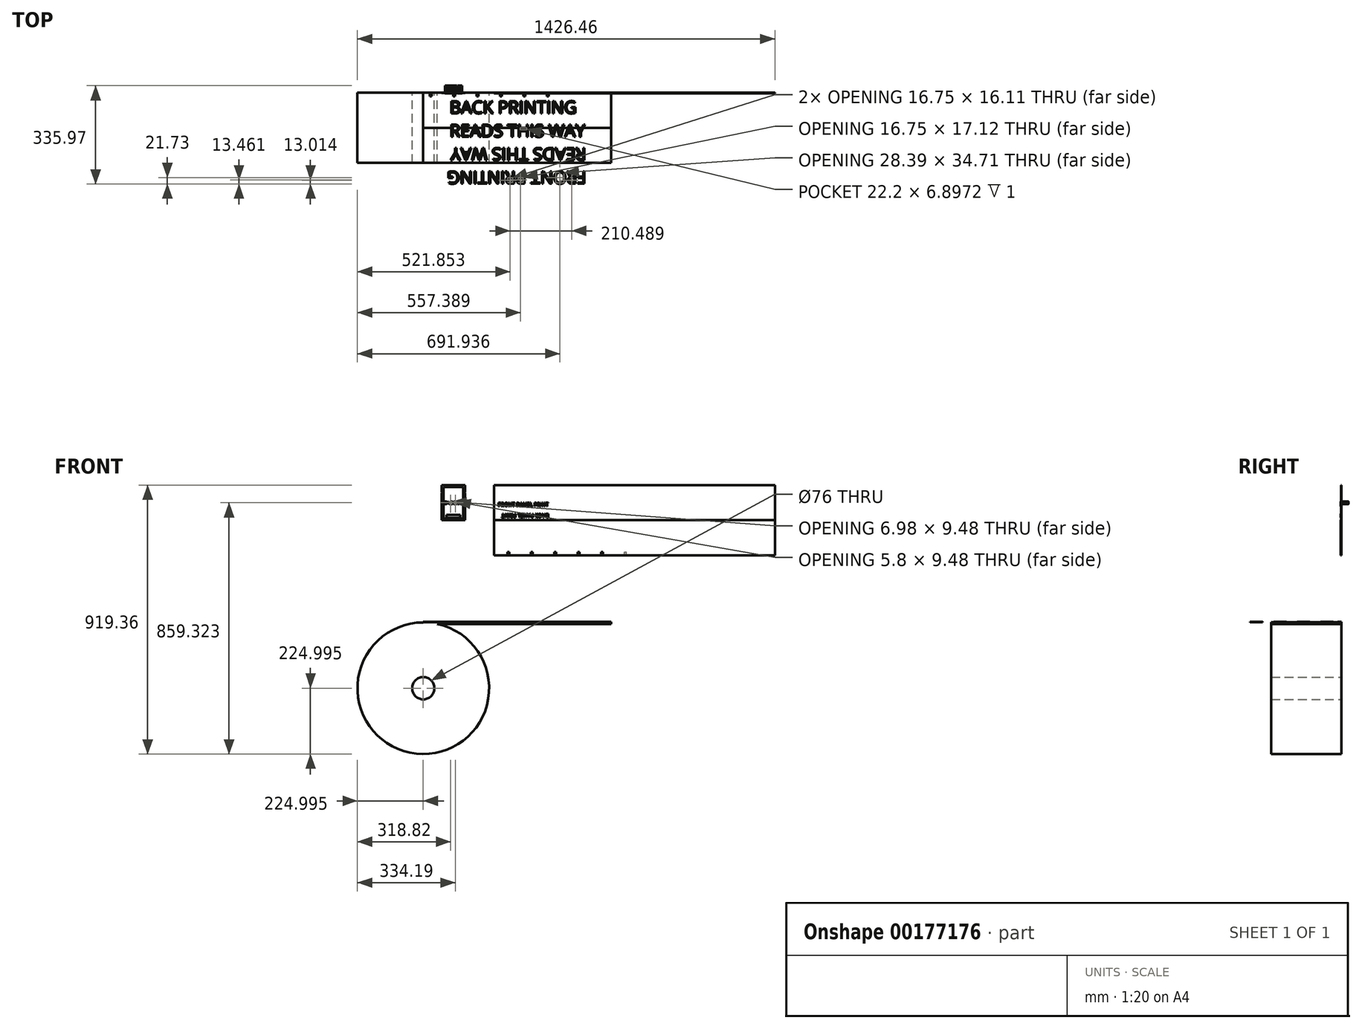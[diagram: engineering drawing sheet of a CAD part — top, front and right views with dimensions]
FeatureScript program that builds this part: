
annotation { "Feature Type Name" : "Feature", "Feature Type Description" : "" }
export const myFeature = defineFeature(function(context is Context, id is Id, definition is map)
    precondition{}
    {
        {
            assignVariable(context, id + "F0", {"name" : "hoogte", "anyValue" : 120});
        }
        {
            var Q0;
            Q0=qCreatedBy(makeId("Front.planeOp"),FACE);
            var sketch = newSketch(context, id + "F1", { "sketchPlane" : qUnion([Q0])});
            skLineSegment(sketch, "E0.bottom", {"start": v(-40, 60) * mm, "end": v(40, 60) * mm});
            skLineSegment(sketch, "E0.top", {"start": v(-40, -60) * mm, "end": v(40, -60) * mm});
            skLineSegment(sketch, "E0.left", {"start": v(-40, 60) * mm, "end": v(-40, -60) * mm});
            skLineSegment(sketch, "E0.right", {"start": v(40, 60) * mm, "end": v(40, -60) * mm});
            skLineSegment(sketch, "E1", {"start": v(-40, 36.41) * mm, "end": v(-38.59, 35) * mm});
            skLineSegment(sketch, "E2", {"start": v(-38.59, 35) * mm, "end": v(-40, 33.59) * mm});
            skLineSegment(sketch, "E3", {"start": v(40, 36.41) * mm, "end": v(38.59, 35) * mm});
            skLineSegment(sketch, "E4", {"start": v(38.59, 35) * mm, "end": v(40, 33.59) * mm});
            skLineSegment(sketch, "E5.bottom", {"start": v(138.46, 60) * mm, "end": v(1098.46, 60) * mm});
            skLineSegment(sketch, "E5.top", {"start": v(138.46, -180) * mm, "end": v(1098.46, -180) * mm});
            skLineSegment(sketch, "E5.left", {"start": v(138.46, 60) * mm, "end": v(138.46, -180) * mm});
            skLineSegment(sketch, "E5.right", {"start": v(1098.46, 60) * mm, "end": v(1098.46, -180) * mm});
            skLineSegment(sketch, "E6", {"start": v(138.46, -60) * mm, "end": v(1098.46, -60) * mm});
            skLineSegment(sketch, "E7", {"start": v(-40, 60) * mm, "end": v(40, -60) * mm, "construction": true});
            skLineSegment(sketch, "E8", {"start": v(40, 60) * mm, "end": v(-40, -60) * mm, "construction": true});
            skPoint(sketch, "E9", {"position": v(0, 0) * mm});
            skSolve(sketch);
        }
        {
            var Q0;
            {var subQ3=sQuery(id+"F1.wireOp",EDGE,"E0.bottom");Q0=makeQuery(id+"F1.imprint","IMPRINT",FACE,{"disambiguationData":[TD([[makeQuery(id+"F1.imprint","IMPRINT",EDGE,{"derivedFrom":subQ3}),-1.0]])]});}
            var Q1;
            Q1=makeQuery(id+"F1.imprint","IMPRINT",FACE,{"disambiguationData":[TD([[makeQuery(id+"F1.imprint","IMPRINT",EDGE,{"derivedFrom":sQuery(id+"F1.wireOp",EDGE,"E5.bottom")}),-1.0]])]});
            var Q2;
            {var subQ0=sQuery(id+"F1.wireOp",EDGE,"E5.top");Q2=makeQuery(id+"F1.imprint","IMPRINT",FACE,{"disambiguationData":[TD([[makeQuery(id+"F1.imprint","IMPRINT",EDGE,{"derivedFrom":subQ0}),1.0]])]});}
            extrude(context, id + "F2", {"entities" : qUnion([Q0, Q1, Q2]), "depth" : 1 * mm});
        }
        {
            var Q0;
            Q0=makeQuery(id+"F2.opExtrude","CAP_FACE",FACE,{"disambiguationData":[OSD([sQuery(id+"F1.wireOp",EDGE,"E0.bottom"),sQuery(id+"F1.wireOp",EDGE,"E0.top"),sQuery(id+"F1.wireOp",EDGE,"E0.left"),sQuery(id+"F1.wireOp",EDGE,"E0.right"),sQuery(id+"F1.wireOp",EDGE,"E1"),sQuery(id+"F1.wireOp",EDGE,"E2"),sQuery(id+"F1.wireOp",EDGE,"E3"),sQuery(id+"F1.wireOp",EDGE,"E4")])],"isStart":false});
            var sketch = newSketch(context, id + "F3", { "sketchPlane" : qUnion([Q0])});
            skLineSegment(sketch, "E10.0.0", {"start": v(40, 60) * mm, "end": v(-40, 60) * mm});
            skLineSegment(sketch, "E10.0.1", {"start": v(-40, 60) * mm, "end": v(-40, 36.41) * mm});
            skLineSegment(sketch, "E10.0.2", {"start": v(-40, 36.41) * mm, "end": v(-38.59, 35) * mm});
            skLineSegment(sketch, "E10.0.3", {"start": v(-38.59, 35) * mm, "end": v(-40, 33.59) * mm});
            skLineSegment(sketch, "E10.0.4", {"start": v(-40, 33.59) * mm, "end": v(-40, -60) * mm});
            skLineSegment(sketch, "E10.0.5", {"start": v(-40, -60) * mm, "end": v(40, -60) * mm});
            skLineSegment(sketch, "E10.0.6", {"start": v(40, -60) * mm, "end": v(40, 33.59) * mm});
            skLineSegment(sketch, "E10.0.7", {"start": v(40, 33.59) * mm, "end": v(38.59, 35) * mm});
            skLineSegment(sketch, "E10.0.8", {"start": v(38.59, 35) * mm, "end": v(40, 36.41) * mm});
            skLineSegment(sketch, "E10.0.9", {"start": v(40, 36.41) * mm, "end": v(40, 60) * mm});
            skLineSegment(sketch, "E11.bottom", {"start": v(-34, 54) * mm, "end": v(34, 54) * mm});
            skLineSegment(sketch, "E11.top", {"start": v(-34, -54) * mm, "end": v(34, -54) * mm});
            skLineSegment(sketch, "E11.left", {"start": v(-34, 54) * mm, "end": v(-34, -54) * mm});
            skLineSegment(sketch, "E11.right", {"start": v(34, 54) * mm, "end": v(34, -54) * mm});
            skLineSegment(sketch, "E12.bottom", {"start": v(-40, 60) * mm, "end": v(-37, 60) * mm});
            skLineSegment(sketch, "E12.top", {"start": v(-40, 48) * mm, "end": v(-37, 48) * mm});
            skLineSegment(sketch, "E12.left", {"start": v(-40, 60) * mm, "end": v(-40, 48) * mm});
            skLineSegment(sketch, "E12.right", {"start": v(-37, 60) * mm, "end": v(-37, 48) * mm});
            skLineSegment(sketch, "E13.bottom", {"start": v(40, 60) * mm, "end": v(37, 60) * mm});
            skLineSegment(sketch, "E13.top", {"start": v(40, 48) * mm, "end": v(37, 48) * mm});
            skLineSegment(sketch, "E13.left", {"start": v(40, 60) * mm, "end": v(40, 48) * mm});
            skLineSegment(sketch, "E13.right", {"start": v(37, 60) * mm, "end": v(37, 48) * mm});
            skLineSegment(sketch, "E14.bottom", {"start": v(-24, -42) * mm, "end": v(24, -42) * mm});
            skLineSegment(sketch, "E14.top", {"start": v(-24, -52) * mm, "end": v(24, -52) * mm});
            skLineSegment(sketch, "E14.left", {"start": v(-24, -42) * mm, "end": v(-24, -52) * mm});
            skLineSegment(sketch, "E14.right", {"start": v(24, -42) * mm, "end": v(24, -52) * mm});
            skSolve(sketch);
        }
        {
            var Q0;
            Q0=makeQuery(id+"F3.imprint","IMPRINT",FACE,{"disambiguationData":[TD([[makeQuery(id+"F3.imprint","IMPRINT",EDGE,{"derivedFrom":sQuery(id+"F3.wireOp",EDGE,"E11.bottom")}),-1.0]])]});
            var Q1;
            Q1=makeQuery(id+"F3.imprint","IMPRINT",FACE,{"disambiguationData":[TD([[makeQuery(id+"F3.imprint","IMPRINT",EDGE,{"derivedFrom":sQuery(id+"F3.wireOp",EDGE,"E12.bottom")}),-1.0]])]});
            var Q2;
            Q2=makeQuery(id+"F3.imprint","IMPRINT",FACE,{"disambiguationData":[TD([[makeQuery(id+"F3.imprint","IMPRINT",EDGE,{"derivedFrom":sQuery(id+"F3.wireOp",EDGE,"E13.bottom")}),-1.0]])]});
            extrude(context, id + "F4", {"entities" : qUnion([Q0, Q1, Q2]), "operationType" : NewBodyOperationType.REMOVE, "oppositeDirection" : true, "depth" : 0.5 * mm});
        }
        {
            var Q0;
            Q0=makeQuery(id+"F2.opExtrude","CAP_FACE",FACE,{"disambiguationData":[OSD([sQuery(id+"F1.wireOp",EDGE,"E5.bottom"),sQuery(id+"F1.wireOp",EDGE,"E5.left"),sQuery(id+"F1.wireOp",EDGE,"E5.right"),sQuery(id+"F1.wireOp",EDGE,"E6")])],"isStart":false});
            var sketch = newSketch(context, id + "F5", { "sketchPlane" : qUnion([Q0])});
            skLineSegment(sketch, "E15.0.0", {"start": v(1098.46, 60) * mm, "end": v(138.46, 60) * mm});
            skLineSegment(sketch, "E15.0.1", {"start": v(138.46, 60) * mm, "end": v(138.46, 60) * mm});
            skLineSegment(sketch, "E15.0.2", {"start": v(138.46, 60) * mm, "end": v(1098.46, 60) * mm});
            skLineSegment(sketch, "E15.0.3", {"start": v(1098.46, 60) * mm, "end": v(1098.46, 60) * mm});
            skLineSegment(sketch, "E16.bottom", {"start": v(184.68, -180) * mm, "end": v(190.68, -180) * mm});
            skLineSegment(sketch, "E16.top", {"start": v(184.68, -168) * mm, "end": v(190.68, -168) * mm});
            skLineSegment(sketch, "E16.left", {"start": v(184.68, -180) * mm, "end": v(184.68, -168) * mm});
            skLineSegment(sketch, "E16.right", {"start": v(190.68, -180) * mm, "end": v(190.68, -168) * mm});
            skLineSegment(sketch, "E17.1.0.0", {"start": v(264.68, -168) * mm, "end": v(270.68, -168) * mm});
            skLineSegment(sketch, "E17.1.0.1", {"start": v(264.68, -180) * mm, "end": v(264.68, -168) * mm});
            skLineSegment(sketch, "E17.1.0.2", {"start": v(264.68, -180) * mm, "end": v(270.68, -180) * mm});
            skLineSegment(sketch, "E17.1.0.3", {"start": v(270.68, -180) * mm, "end": v(270.68, -168) * mm});
            skLineSegment(sketch, "E17.2.0.0", {"start": v(344.68, -168) * mm, "end": v(350.68, -168) * mm});
            skLineSegment(sketch, "E17.2.0.1", {"start": v(344.68, -180) * mm, "end": v(344.68, -168) * mm});
            skLineSegment(sketch, "E17.2.0.2", {"start": v(344.68, -180) * mm, "end": v(350.68, -180) * mm});
            skLineSegment(sketch, "E17.2.0.3", {"start": v(350.68, -180) * mm, "end": v(350.68, -168) * mm});
            skLineSegment(sketch, "E17.direction1", {"start": v(184.68, -180) * mm, "end": v(264.68, -180) * mm, "construction": true});
            skLineSegment(sketch, "E18.0.3.0", {"start": v(424.68, -168) * mm, "end": v(430.68, -168) * mm});
            skLineSegment(sketch, "E18.3.3.0", {"start": v(424.68, -180) * mm, "end": v(424.68, -168) * mm});
            skLineSegment(sketch, "E18.6.3.0", {"start": v(424.68, -180) * mm, "end": v(430.68, -180) * mm});
            skLineSegment(sketch, "E18.9.3.0", {"start": v(430.68, -180) * mm, "end": v(430.68, -168) * mm});
            skLineSegment(sketch, "E18.0.4.0", {"start": v(504.68, -168) * mm, "end": v(510.68, -168) * mm});
            skLineSegment(sketch, "E18.3.4.0", {"start": v(504.68, -180) * mm, "end": v(504.68, -168) * mm});
            skLineSegment(sketch, "E18.6.4.0", {"start": v(504.68, -180) * mm, "end": v(510.68, -180) * mm});
            skLineSegment(sketch, "E18.9.4.0", {"start": v(510.68, -180) * mm, "end": v(510.68, -168) * mm});
            skLineSegment(sketch, "E19.0.5.0", {"start": v(584.68, -168) * mm, "end": v(590.68, -168) * mm});
            skLineSegment(sketch, "E19.3.5.0", {"start": v(584.68, -180) * mm, "end": v(584.68, -168) * mm});
            skLineSegment(sketch, "E19.6.5.0", {"start": v(584.68, -180) * mm, "end": v(590.68, -180) * mm});
            skLineSegment(sketch, "E19.9.5.0", {"start": v(590.68, -180) * mm, "end": v(590.68, -168) * mm});
            skSolve(sketch);
        }
        {
            var Q0;
            Q0=makeQuery(id+"F5.imprint","IMPRINT",FACE,{"disambiguationData":[TD([[makeQuery(id+"F5.imprint","IMPRINT",EDGE,{"derivedFrom":sQuery(id+"F5.wireOp",EDGE,"JLQzprwf-iRJq-cmRX-vWmS-HmgRmsplr5sc.top")}),-1.0]])]});
            var Q1;
            Q1=makeQuery(id+"F5.imprint","IMPRINT",FACE,{"disambiguationData":[TD([[makeQuery(id+"F5.imprint","IMPRINT",EDGE,{"derivedFrom":sQuery(id+"F5.wireOp",EDGE,"E16.bottom")}),1.0]])]});
            var Q2;
            Q2=makeQuery(id+"F5.imprint","IMPRINT",FACE,{"disambiguationData":[TD([[makeQuery(id+"F5.imprint","IMPRINT",EDGE,{"derivedFrom":sQuery(id+"F5.wireOp",EDGE,"E17.1.0.0")}),-1.0]])]});
            var Q3;
            Q3=makeQuery(id+"F5.imprint","IMPRINT",FACE,{"disambiguationData":[TD([[makeQuery(id+"F5.imprint","IMPRINT",EDGE,{"derivedFrom":sQuery(id+"F5.wireOp",EDGE,"E17.2.0.0")}),-1.0]])]});
            var Q4;
            Q4=makeQuery(id+"F5.imprint","IMPRINT",FACE,{"disambiguationData":[TD([[makeQuery(id+"F5.imprint","IMPRINT",EDGE,{"derivedFrom":sQuery(id+"F5.wireOp",EDGE,"E18.0.3.0")}),-1.0]])]});
            var Q5;
            Q5=makeQuery(id+"F5.imprint","IMPRINT",FACE,{"disambiguationData":[TD([[makeQuery(id+"F5.imprint","IMPRINT",EDGE,{"derivedFrom":sQuery(id+"F5.wireOp",EDGE,"E18.0.4.0")}),-1.0]])]});
            var Q6;
            Q6=makeQuery(id+"F5.imprint","IMPRINT",FACE,{"disambiguationData":[TD([[makeQuery(id+"F5.imprint","IMPRINT",EDGE,{"derivedFrom":sQuery(id+"F5.wireOp",EDGE,"E19.0.5.0")}),-1.0]])]});
            extrude(context, id + "F6", {"entities" : qUnion([Q0, Q1, Q2, Q3, Q4, Q5, Q6]), "operationType" : NewBodyOperationType.REMOVE, "oppositeDirection" : true, "depth" : 0.5 * mm});
        }
        {
            var Q0;
            Q0=qCreatedBy(makeId("Front.planeOp"),FACE);
            var sketch = newSketch(context, id + "F7", { "sketchPlane" : qUnion([Q0])});
            skCircle(sketch, "E20", {"center": v(-103, -634.36) * mm, "radius": 225 * mm});
            skLineSegment(sketch, "E21.bottom", {"start": v(-103, -408.35) * mm, "end": v(538.87, -408.35) * mm});
            skLineSegment(sketch, "E21.top", {"start": v(-103, -414.51) * mm, "end": v(538.87, -414.51) * mm});
            skLineSegment(sketch, "E21.left", {"start": v(-103, -414.51) * mm, "end": v(-103, -408.35) * mm});
            skLineSegment(sketch, "E21.right", {"start": v(538.87, -414.51) * mm, "end": v(538.87, -408.35) * mm});
            skCircle(sketch, "E22", {"center": v(-103, -634.36) * mm, "radius": 38 * mm});
            skSolve(sketch);
        }
        {
            var Q0;
            Q0=qSketchRegion(id+"F7",true);
            extrude(context, id + "F8", {"entities" : qUnion([Q0]), "depth" : (((getVariable(context, 'hoogte')) * 2)) * mm});
        }
        {
            var Q0;
            {var subQ0=sQuery(id+"F1.wireOp",EDGE,"E4");var subQ1=sQuery(id+"F1.wireOp",EDGE,"E2");var subQ2=sQuery(id+"F1.wireOp",EDGE,"E1");var subQ3=sQuery(id+"F1.wireOp",EDGE,"E0.right");var subQ4=sQuery(id+"F1.wireOp",EDGE,"E0.top");var subQ5=sQuery(id+"F1.wireOp",EDGE,"E0.bottom");var subQ6=sQuery(id+"F1.wireOp",EDGE,"E3");var subQ7=sQuery(id+"F1.wireOp",EDGE,"E0.left");Q0=makeQuery(id+"F4.boolean.opBoolean","SPLIT",FACE,{"disambiguationData":[TD([makeQuery(id+"F2.opExtrude","SWEPT_FACE",FACE,{"disambiguationData":[OSD([subQ5])]})])],"derivedFrom":makeQuery(id+"F2.opExtrude","CAP_FACE",FACE,{"disambiguationData":[OSD([subQ5,subQ4,subQ7,subQ3,subQ2,subQ1,subQ6,subQ0])],"isStart":false})});}
            var sketch = newSketch(context, id + "F9", { "sketchPlane" : qUnion([Q0])});
            skText(sketch, "E23", { "text": "BACKSIDE", "fontName": "OpenSans-Regular.ttf"});
            const initialGuessF9  = {"E23": [-0.03, -0.00465, 1, 0, 0.0093]};
            skSetInitialGuess(sketch, initialGuessF9);
            skSolve(sketch);
        }
        {
            var Q0;
            Q0=qSketchRegion(id+"F9",true);
            extrude(context, id + "F10", {"entities" : qUnion([Q0]), "operationType" : NewBodyOperationType.ADD, "depth" : 1 * mm, "hasSecondDirection" : true, "secondDirectionOppositeDirection" : true, "secondDirectionDepth" : 25 * mm});
        }
        {
            var Q0;
            {var subQ0=sQuery(id+"F1.wireOp",EDGE,"E5.bottom");var subQ1=sQuery(id+"F1.wireOp",EDGE,"E5.left");var subQ2=sQuery(id+"F1.wireOp",EDGE,"E5.right");Q0=makeQuery(id+"F6.boolean.opBoolean","SPLIT",FACE,{"disambiguationData":[TD([makeQuery(id+"F2.opExtrude","SWEPT_FACE",FACE,{"disambiguationData":[OSD([subQ0])]})])],"derivedFrom":makeQuery(id+"F2.opExtrude","CAP_FACE",FACE,{"disambiguationData":[OSD([subQ0,sQuery(id+"F1.wireOp",EDGE,"E5.top"),subQ1,subQ2])],"isStart":false})});}
            var sketch = newSketch(context, id + "F11", { "sketchPlane" : qUnion([Q0])});
            skText(sketch, "E24", { "text": "FRONT PANEL PRINT", "fontName": "AllertaStencil-Regular.ttf"});
            skLineSegment(sketch, "E25.0.0", {"start": v(1098.46, -60) * mm, "end": v(138.46, -60) * mm});
            skLineSegment(sketch, "E25.0.1", {"start": v(138.46, -60) * mm, "end": v(138.46, -180) * mm});
            skLineSegment(sketch, "E25.0.2", {"start": v(138.46, -180) * mm, "end": v(184.68, -180) * mm});
            skLineSegment(sketch, "E25.0.3", {"start": v(184.68, -180) * mm, "end": v(184.68, -168) * mm});
            skLineSegment(sketch, "E25.0.4", {"start": v(184.68, -168) * mm, "end": v(190.68, -168) * mm});
            skLineSegment(sketch, "E25.0.5", {"start": v(190.68, -168) * mm, "end": v(190.68, -180) * mm});
            skLineSegment(sketch, "E25.0.6", {"start": v(190.68, -180) * mm, "end": v(264.68, -180) * mm});
            skLineSegment(sketch, "E25.0.7", {"start": v(264.68, -180) * mm, "end": v(264.68, -168) * mm});
            skLineSegment(sketch, "E25.0.8", {"start": v(264.68, -168) * mm, "end": v(270.68, -168) * mm});
            skLineSegment(sketch, "E25.0.9", {"start": v(270.68, -168) * mm, "end": v(270.68, -180) * mm});
            skLineSegment(sketch, "E25.0.10", {"start": v(270.68, -180) * mm, "end": v(344.68, -180) * mm});
            skLineSegment(sketch, "E25.0.11", {"start": v(344.68, -180) * mm, "end": v(344.68, -168) * mm});
            skLineSegment(sketch, "E25.0.12", {"start": v(344.68, -168) * mm, "end": v(350.68, -168) * mm});
            skLineSegment(sketch, "E25.0.13", {"start": v(350.68, -168) * mm, "end": v(350.68, -180) * mm});
            skLineSegment(sketch, "E25.0.14", {"start": v(350.68, -180) * mm, "end": v(424.68, -180) * mm});
            skLineSegment(sketch, "E25.0.15", {"start": v(424.68, -180) * mm, "end": v(424.68, -168) * mm});
            skLineSegment(sketch, "E25.0.16", {"start": v(424.68, -168) * mm, "end": v(430.68, -168) * mm});
            skLineSegment(sketch, "E25.0.17", {"start": v(430.68, -168) * mm, "end": v(430.68, -180) * mm});
            skLineSegment(sketch, "E25.0.18", {"start": v(430.68, -180) * mm, "end": v(504.68, -180) * mm});
            skLineSegment(sketch, "E25.0.19", {"start": v(504.68, -180) * mm, "end": v(504.68, -168) * mm});
            skLineSegment(sketch, "E25.0.20", {"start": v(504.68, -168) * mm, "end": v(510.68, -168) * mm});
            skLineSegment(sketch, "E25.0.21", {"start": v(510.68, -168) * mm, "end": v(510.68, -180) * mm});
            skLineSegment(sketch, "E25.0.22", {"start": v(510.68, -180) * mm, "end": v(1098.46, -180) * mm});
            skLineSegment(sketch, "E25.0.23", {"start": v(1098.46, -180) * mm, "end": v(1098.46, -60) * mm});
            skText(sketch, "E26", { "text": "BACK PANEL PRINT", "fontName": "AllertaStencil-Regular.ttf"});
            skLineSegment(sketch, "E27", {"start": v(1068.46, -120) * mm, "end": v(1068.46, -121.37) * mm});
            const initialGuessF11  = {"E24": [0.1529, -0.0125, 1, 0, 0.0125], "E26": [0.32596, -0.0375, -1, 0, 0.0125]};
            skSetInitialGuess(sketch, initialGuessF11);
            skSolve(sketch);
        }
        {
            var Q0;
            Q0 = qSketchRegion(id + "F11", true);
            extrude(context, id + "F12", {"entities" : qUnion([Q0]), "operationType" : NewBodyOperationType.ADD, "depth" : 1 * mm});
        }
        {
            var Q0;
            Q0=makeQuery(id+"F8.opExtrude","SWEPT_FACE",FACE,{"disambiguationData":[OSD([sQuery(id+"F7.wireOp",EDGE,"E21.bottom")])]});
            var sketch = newSketch(context, id + "F13", { "sketchPlane" : qUnion([Q0])});
            skText(sketch, "E28", { "text": "BACK PRINTING \nREADS THIS WAY", "fontName": "OpenSans-Regular.ttf"});
            skText(sketch, "E29", { "text": "FRONT PRINTING\nREADS THIS WAY", "fontName": "OpenSans-Regular.ttf"});
            skLineSegment(sketch, "E30", {"start": v(478.87, -157.44) * mm, "end": v(478.87, -220) * mm});
            skLineSegment(sketch, "E31", {"start": v(538.87, -120) * mm, "end": v(-103, -120) * mm, "construction": true});
            skLineSegment(sketch, "E32.bottom", {"start": v(538.87, -120) * mm, "end": v(-103, -120) * mm});
            skLineSegment(sketch, "E32.top", {"start": v(538.87, -119.95) * mm, "end": v(-103, -119.95) * mm});
            skLineSegment(sketch, "E32.left", {"start": v(538.87, -120) * mm, "end": v(538.87, -119.95) * mm});
            skLineSegment(sketch, "E32.right", {"start": v(-103, -120) * mm, "end": v(-103, -119.95) * mm});
            skLineSegment(sketch, "E33.bottom", {"start": v(538.87, -120.05) * mm, "end": v(-103, -120.05) * mm});
            skLineSegment(sketch, "E33.left", {"start": v(538.87, -120.05) * mm, "end": v(538.87, -120) * mm});
            skLineSegment(sketch, "E33.right", {"start": v(-103, -120.05) * mm, "end": v(-103, -120) * mm});
            skLineSegment(sketch, "E34.bottom", {"start": v(-80.23, 0) * mm, "end": v(-74.23, 0) * mm});
            skLineSegment(sketch, "E34.top", {"start": v(-80.23, -12) * mm, "end": v(-74.23, -12) * mm});
            skLineSegment(sketch, "E34.left", {"start": v(-80.23, 0) * mm, "end": v(-80.23, -12) * mm});
            skLineSegment(sketch, "E34.right", {"start": v(-74.23, 0) * mm, "end": v(-74.23, -12) * mm});
            skLineSegment(sketch, "E35.1.0.0", {"start": v(-0.23, 0) * mm, "end": v(5.77, 0) * mm});
            skLineSegment(sketch, "E35.1.0.1", {"start": v(-0.23, -12) * mm, "end": v(5.77, -12) * mm});
            skLineSegment(sketch, "E35.1.0.2", {"start": v(-0.23, 0) * mm, "end": v(-0.23, -12) * mm});
            skLineSegment(sketch, "E35.1.0.3", {"start": v(5.77, 0) * mm, "end": v(5.77, -12) * mm});
            skLineSegment(sketch, "E35.2.0.0", {"start": v(79.77, 0) * mm, "end": v(85.77, 0) * mm});
            skLineSegment(sketch, "E35.2.0.1", {"start": v(79.77, -12) * mm, "end": v(85.77, -12) * mm});
            skLineSegment(sketch, "E35.2.0.2", {"start": v(79.77, 0) * mm, "end": v(79.77, -12) * mm});
            skLineSegment(sketch, "E35.2.0.3", {"start": v(85.77, 0) * mm, "end": v(85.77, -12) * mm});
            skLineSegment(sketch, "E35.direction1", {"start": v(-80.23, -12) * mm, "end": v(-0.23, -12) * mm, "construction": true});
            skLineSegment(sketch, "E36.0.3.0", {"start": v(159.77, 0) * mm, "end": v(165.77, 0) * mm});
            skLineSegment(sketch, "E36.3.3.0", {"start": v(159.77, -12) * mm, "end": v(165.77, -12) * mm});
            skLineSegment(sketch, "E36.6.3.0", {"start": v(159.77, 0) * mm, "end": v(159.77, -12) * mm});
            skLineSegment(sketch, "E36.9.3.0", {"start": v(165.77, 0) * mm, "end": v(165.77, -12) * mm});
            skLineSegment(sketch, "E36.0.4.0", {"start": v(239.77, 0) * mm, "end": v(245.77, 0) * mm});
            skLineSegment(sketch, "E36.3.4.0", {"start": v(239.77, -12) * mm, "end": v(245.77, -12) * mm});
            skLineSegment(sketch, "E36.6.4.0", {"start": v(239.77, 0) * mm, "end": v(239.77, -12) * mm});
            skLineSegment(sketch, "E36.9.4.0", {"start": v(245.77, 0) * mm, "end": v(245.77, -12) * mm});
            skLineSegment(sketch, "E36.0.5.0", {"start": v(319.77, 0) * mm, "end": v(325.77, 0) * mm});
            skLineSegment(sketch, "E36.3.5.0", {"start": v(319.77, -12) * mm, "end": v(325.77, -12) * mm});
            skLineSegment(sketch, "E36.6.5.0", {"start": v(319.77, 0) * mm, "end": v(319.77, -12) * mm});
            skLineSegment(sketch, "E36.9.5.0", {"start": v(325.77, 0) * mm, "end": v(325.77, -12) * mm});
            const initialGuessF13  = {"E28": [-0.01285, -0.07083, 1, 0, 0.0425], "E29": [0.45387, -0.26917, -1, 0, 0.0425]};
            skSetInitialGuess(sketch, initialGuessF13);
            skSolve(sketch);
        }
        {
            var Q0;
            Q0=qSketchRegion(id+"F13",true);
            extrude(context, id + "F14", {"entities" : qUnion([Q0]), "operationType" : NewBodyOperationType.ADD, "depth" : 1 * mm});
        }
    });
